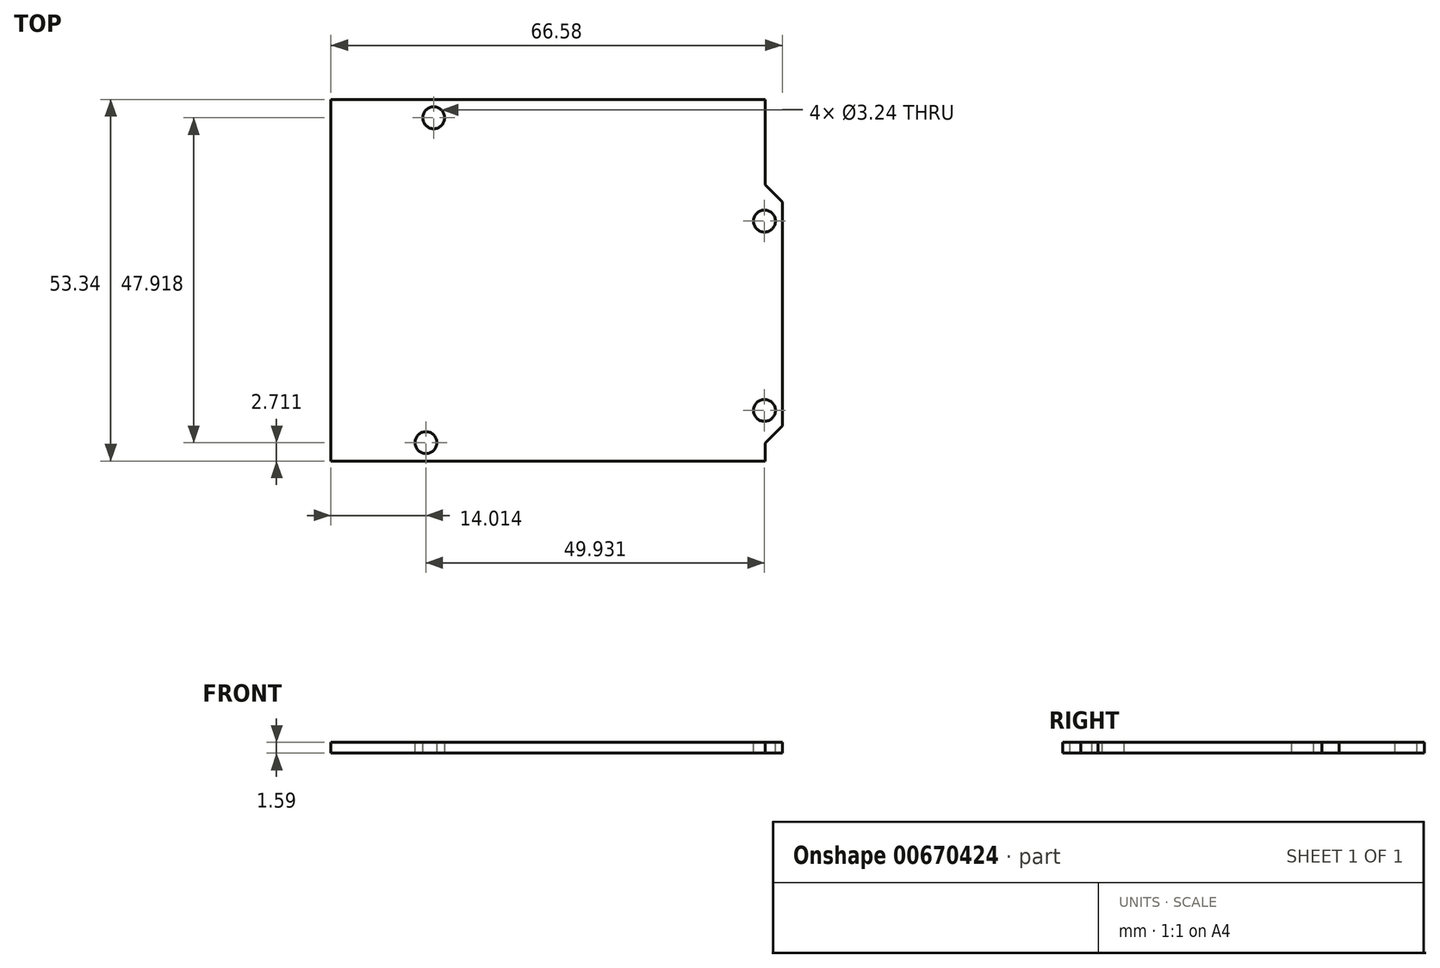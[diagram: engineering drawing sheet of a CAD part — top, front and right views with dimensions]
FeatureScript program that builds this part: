
annotation { "Feature Type Name" : "Feature", "Feature Type Description" : "" }
export const myFeature = defineFeature(function(context is Context, id is Id, definition is map)
    precondition{}
    {
        {
            var Q0;
            Q0=qCreatedBy(makeId("Top.planeOp"),FACE);
            var sketch = newSketch(context, id + "F0", { "sketchPlane" : qUnion([Q0])});
            skLineSegment(sketch, "E0.bottom", {"start": v(-32.02, 26.67) * mm, "end": v(32.02, 26.67) * mm});
            skLineSegment(sketch, "E0.top", {"start": v(-32.02, -26.67) * mm, "end": v(32.02, -26.67) * mm});
            skLineSegment(sketch, "E0.left", {"start": v(-32.02, 26.67) * mm, "end": v(-32.02, -26.67) * mm});
            skLineSegment(sketch, "E0.right", {"start": v(32.02, 26.67) * mm, "end": v(32.02, 14.1) * mm});
            skPoint(sketch, "E0.middle", {"position": v(0, 0) * mm});
            skLineSegment(sketch, "E1", {"start": v(32.02, -24) * mm, "end": v(34.56, -21.46) * mm});
            skLineSegment(sketch, "E2", {"start": v(34.56, -21.46) * mm, "end": v(34.56, 11.56) * mm});
            skLineSegment(sketch, "E3", {"start": v(34.56, 11.56) * mm, "end": v(32.02, 14.1) * mm});
            skLineSegment(sketch, "E4.trimOffspring", {"start": v(32.02, -24) * mm, "end": v(32.02, -26.67) * mm});
            skSolve(sketch);
        }
        {
            var Q0;
            Q0 = qSketchRegion(id + "F0", true);
            extrude(context, id + "F1", {"entities" : qUnion([Q0]), "depth" : 1.59 * mm, "offsetDistance" : 25 * mm});
        }
        {
            var Q0;
            Q0=makeQuery(id+"F1.opExtrude","CAP_FACE",FACE,{"disambiguationData":[OSD([sQuery(id+"F0.wireOp",EDGE,"E0.bottom"),sQuery(id+"F0.wireOp",EDGE,"E0.top"),sQuery(id+"F0.wireOp",EDGE,"E0.left"),sQuery(id+"F0.wireOp",EDGE,"E0.right"),sQuery(id+"F0.wireOp",EDGE,"E1"),sQuery(id+"F0.wireOp",EDGE,"E2"),sQuery(id+"F0.wireOp",EDGE,"E3"),sQuery(id+"F0.wireOp",EDGE,"E4.trimOffspring")])],"isStart":false});
            var sketch = newSketch(context, id + "F2", { "sketchPlane" : qUnion([Q0])});
            skCircle(sketch, "E5", {"center": v(-16.86, 23.96) * mm, "radius": 1.62 * mm});
            skCircle(sketch, "E6", {"center": v(31.92, 8.72) * mm, "radius": 1.62 * mm});
            skCircle(sketch, "E7", {"center": v(-18, -23.96) * mm, "radius": 1.62 * mm});
            skCircle(sketch, "E8", {"center": v(31.92, -19.2) * mm, "radius": 1.62 * mm});
            skSolve(sketch);
        }
        {
            var Q0;
            Q0 = qSketchRegion(id + "F2", true);
            extrude(context, id + "F3", {"entities" : qUnion([Q0]), "operationType" : NewBodyOperationType.REMOVE, "oppositeDirection" : true, "depth" : 25 * mm, "offsetDistance" : 25 * mm});
        }
    });
